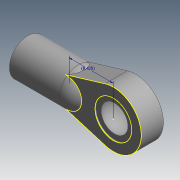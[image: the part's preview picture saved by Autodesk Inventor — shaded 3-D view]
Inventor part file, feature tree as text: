
AUTODESK INVENTOR PART (.ipt)
format: ipt  version: 2014 SP1 (Build 180222100, 222)  size: 141,824 bytes
history: native  units: in
note: dims shown in document units (in); Inventor stores cm internally (conversion verified against a paired STEP export)
features: sketch x7, extrude x5, revolve x1, fillet x1, boolean_combine x1
ambient origin geometry x8: Origin, YZ Plane, XZ Plane, XY Plane, X Axis, Y Axis, Z Axis, Center Point
bodies: Solid1 (feature_tree), Solid2 (feature_tree)
feature tree (15):
  sketch  "Sketch1"  dims[d0=0.4193in d2=0.2756in]
  extrude  "Extrusion1"  Depth=0.2756in
  extrude  "Extrusion2"  Depth=0.1673in
  revolve  "Revolution1"  [1 undecoded]
  extrude  "Extrusion3"  Depth=0.2756in
  extrude  "Extrusion4"  Depth=0.2096in TaperAngle=0.0deg
  fillet  "Fillet1"  Radius=0.1378in
  boolean_combine  "Combine1"
  extrude  "Extrusion5"  Depth=0.3937in TaperAngle=0.0deg
  sketch  "Sketch7"  dims[d19=0.7254in]
  sketch  "Sketch2"  dims[d3=0.1673in d4=0.0in d5=0.2756in]
  sketch  "Sketch3"  dims[d6=0.1476in d7=0.0in d8=0.25in]
  sketch  "Sketch4"  dims[d9=360.0deg d10=0.2756in]
  sketch  "Sketch5"  dims[d11=0.3937in d12=0.0in d13=0.2096in d14=0.0in d15=0.1378in]
  sketch  "Sketch6"  dims[d16=0.1299in d17=0.3937in d18=0.0in]
note: 1 required parameter value undecoded (feature->parameter linkage not recoverable at this tier; creation-order binding heuristic only, values carry confidence <= 0.55)
